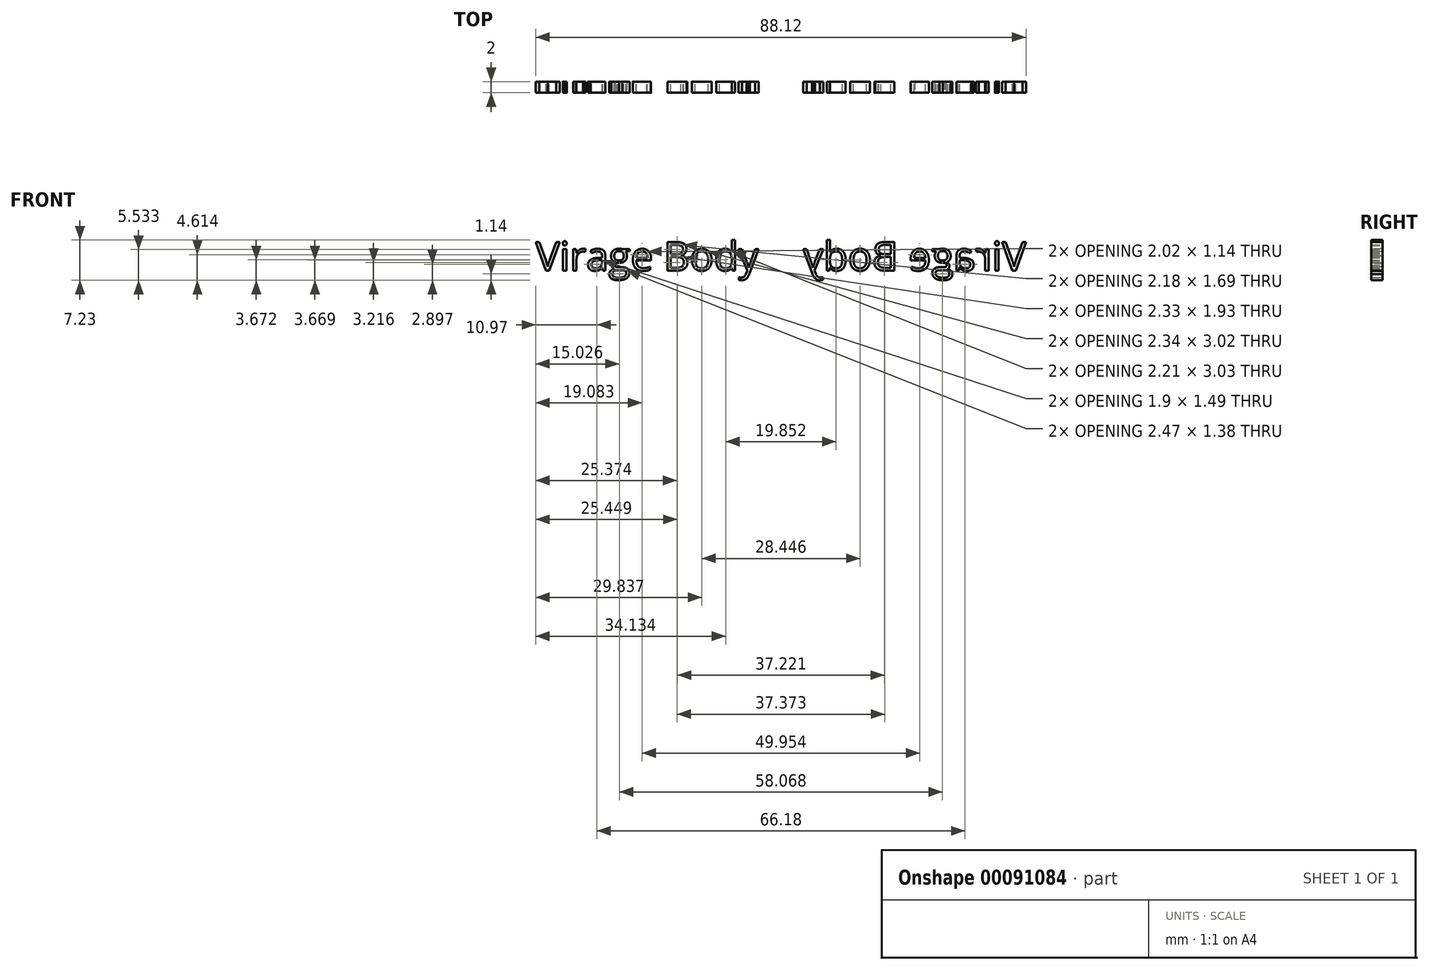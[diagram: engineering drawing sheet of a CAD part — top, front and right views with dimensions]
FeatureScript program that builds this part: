
annotation { "Feature Type Name" : "Feature", "Feature Type Description" : "" }
export const myFeature = defineFeature(function(context is Context, id is Id, definition is map)
    precondition{}
    {
        {
            var Q0;
            Q0=qCreatedBy(makeId("Front.planeOp"),FACE);
            var sketch = newSketch(context, id + "F0", { "sketchPlane" : qUnion([Q0])});
            skText(sketch, "E0", { "text": "Virage Body", "fontName": "OpenSans-Regular.ttf"});
            skLineSegment(sketch, "E1", {"start": v(0, 10.9) * mm, "end": v(0, 9.35) * mm, "construction": true});
            skLineSegment(sketch, "E2", {"start": v(0, 9.35) * mm, "end": v(0, -9.41) * mm, "construction": true});
            skLineSegment(sketch, "E3.MirrorCS", {"start": v(0, -4.2) * mm, "end": v(0, 14.57) * mm, "construction": true});
            const initialGuessF0  = {"E0": [-0.04406, -0.00261, 1, 0, 0.0052]};
            skSetInitialGuess(sketch, initialGuessF0);
            skSolve(sketch);
        }
        {
            var Q0;
            Q0 = qSketchRegion(id + "F0", true);
            extrude(context, id + "F1", {"entities" : qUnion([Q0]), "depth" : 2 * mm});
        }
        {
            var Q0;
            Q0=makeQuery(id+"F1.opExtrude","SWEPT_BODY",BODY,{"disambiguationData":[OSD([sQuery(id+"F0.wireOp",EDGE,"E0.sketch_text.stroke-104"),sQuery(id+"F0.wireOp",EDGE,"E0.sketch_text.stroke-105"),sQuery(id+"F0.wireOp",EDGE,"E0.sketch_text.stroke-106"),sQuery(id+"F0.wireOp",EDGE,"E0.sketch_text.stroke-107")])]});
            var Q1;
            Q1=makeQuery(id+"F1.opExtrude","SWEPT_FACE",FACE,{"disambiguationData":[OSD([sQuery(id+"F0.wireOp",EDGE,"E0.sketch_text.stroke-55")])]});
            var Q2;
            Q2=makeQuery(id+"F1.opExtrude","SWEPT_FACE",FACE,{"disambiguationData":[OSD([sQuery(id+"F0.wireOp",EDGE,"E0.sketch_text.stroke-92")])]});
            var Q3;
            Q3=makeQuery(id+"F1.opExtrude","SWEPT_FACE",FACE,{"disambiguationData":[OSD([sQuery(id+"F0.wireOp",EDGE,"E0.sketch_text.stroke-93")])]});
            var Q4;
            Q4=makeQuery(id+"F1.opExtrude","SWEPT_FACE",FACE,{"disambiguationData":[OSD([sQuery(id+"F0.wireOp",EDGE,"E0.sketch_text.stroke-103")])]});
            var Q5;
            Q5=makeQuery(id+"F1.opExtrude","SWEPT_FACE",FACE,{"disambiguationData":[OSD([sQuery(id+"F0.wireOp",EDGE,"E0.sketch_text.stroke-106")])]});
            var Q6;
            Q6=makeQuery(id+"F1.opExtrude","CAP_FACE",FACE,{"disambiguationData":[OSD([sQuery(id+"F0.wireOp",EDGE,"E0.sketch_text.stroke-105"),sQuery(id+"F0.wireOp",EDGE,"E0.sketch_text.stroke-106"),sQuery(id+"F0.wireOp",EDGE,"E0.sketch_text.stroke-107"),sQuery(id+"F0.wireOp",EDGE,"E0.sketch_text.stroke-108"),sQuery(id+"F0.wireOp",EDGE,"E0.sketch_text.stroke-109"),sQuery(id+"F0.wireOp",EDGE,"E0.sketch_text.stroke-110"),sQuery(id+"F0.wireOp",EDGE,"E0.sketch_text.stroke-111"),sQuery(id+"F0.wireOp",EDGE,"E0.sketch_text.stroke-112"),sQuery(id+"F0.wireOp",EDGE,"E0.sketch_text.stroke-113"),sQuery(id+"F0.wireOp",EDGE,"E0.sketch_text.stroke-114"),sQuery(id+"F0.wireOp",EDGE,"E0.sketch_text.stroke-115"),sQuery(id+"F0.wireOp",EDGE,"E0.sketch_text.stroke-116"),sQuery(id+"F0.wireOp",EDGE,"E0.sketch_text.stroke-117"),sQuery(id+"F0.wireOp",EDGE,"E0.sketch_text.stroke-118"),sQuery(id+"F0.wireOp",EDGE,"E0.sketch_text.stroke-119"),sQuery(id+"F0.wireOp",EDGE,"E0.sketch_text.stroke-120"),sQuery(id+"F0.wireOp",EDGE,"E0.sketch_text.stroke-121"),sQuery(id+"F0.wireOp",EDGE,"E0.sketch_text.stroke-122"),sQuery(id+"F0.wireOp",EDGE,"E0.sketch_text.stroke-123")])],"isStart":true});
            var Q7;
            Q7=makeQuery(id+"F1.opExtrude","SWEPT_FACE",FACE,{"disambiguationData":[OSD([sQuery(id+"F0.wireOp",EDGE,"E0.sketch_text.stroke-162")])]});
            var Q8;
            Q8=makeQuery(id+"F1.opExtrude","CAP_FACE",FACE,{"disambiguationData":[OSD([sQuery(id+"F0.wireOp",EDGE,"E0.sketch_text.stroke-149"),sQuery(id+"F0.wireOp",EDGE,"E0.sketch_text.stroke-150"),sQuery(id+"F0.wireOp",EDGE,"E0.sketch_text.stroke-151"),sQuery(id+"F0.wireOp",EDGE,"E0.sketch_text.stroke-152"),sQuery(id+"F0.wireOp",EDGE,"E0.sketch_text.stroke-153"),sQuery(id+"F0.wireOp",EDGE,"E0.sketch_text.stroke-154"),sQuery(id+"F0.wireOp",EDGE,"E0.sketch_text.stroke-155"),sQuery(id+"F0.wireOp",EDGE,"E0.sketch_text.stroke-156"),sQuery(id+"F0.wireOp",EDGE,"E0.sketch_text.stroke-157"),sQuery(id+"F0.wireOp",EDGE,"E0.sketch_text.stroke-158"),sQuery(id+"F0.wireOp",EDGE,"E0.sketch_text.stroke-159"),sQuery(id+"F0.wireOp",EDGE,"E0.sketch_text.stroke-160"),sQuery(id+"F0.wireOp",EDGE,"E0.sketch_text.stroke-161"),sQuery(id+"F0.wireOp",EDGE,"E0.sketch_text.stroke-162"),sQuery(id+"F0.wireOp",EDGE,"E0.sketch_text.stroke-163"),sQuery(id+"F0.wireOp",EDGE,"E0.sketch_text.stroke-164"),sQuery(id+"F0.wireOp",EDGE,"E0.sketch_text.stroke-165")])],"isStart":false});
            var Q9;
            Q9=makeQuery(id+"F1.opExtrude","SWEPT_FACE",FACE,{"disambiguationData":[OSD([sQuery(id+"F0.wireOp",EDGE,"E0.sketch_text.stroke-163")])]});
            var Q10;
            Q10=makeQuery(id+"F1.opExtrude","SWEPT_FACE",FACE,{"disambiguationData":[OSD([sQuery(id+"F0.wireOp",EDGE,"E0.sketch_text.stroke-147")])]});
            var Q11;
            Q11=makeQuery(id+"F1.opExtrude","SWEPT_FACE",FACE,{"disambiguationData":[OSD([sQuery(id+"F0.wireOp",EDGE,"E0.sketch_text.stroke-148")])]});
            var Q12;
            Q12=makeQuery(id+"F1.opExtrude","SWEPT_FACE",FACE,{"disambiguationData":[OSD([sQuery(id+"F0.wireOp",EDGE,"E0.sketch_text.stroke-149")])]});
            var Q13;
            Q13=makeQuery(id+"F1.opExtrude","SWEPT_FACE",FACE,{"disambiguationData":[OSD([sQuery(id+"F0.wireOp",EDGE,"E0.sketch_text.stroke-150")])]});
            var Q14;
            Q14=makeQuery(id+"F1.opExtrude","SWEPT_FACE",FACE,{"disambiguationData":[OSD([sQuery(id+"F0.wireOp",EDGE,"E0.sketch_text.stroke-151")])]});
            var Q15;
            Q15=makeQuery(id+"F1.opExtrude","SWEPT_FACE",FACE,{"disambiguationData":[OSD([sQuery(id+"F0.wireOp",EDGE,"E0.sketch_text.stroke-155")])]});
            var Q16;
            Q16=makeQuery(id+"F1.opExtrude","SWEPT_FACE",FACE,{"disambiguationData":[OSD([sQuery(id+"F0.wireOp",EDGE,"E0.sketch_text.stroke-156")])]});
            var Q17;
            Q17=makeQuery(id+"F1.opExtrude","SWEPT_FACE",FACE,{"disambiguationData":[OSD([sQuery(id+"F0.wireOp",EDGE,"E0.sketch_text.stroke-158")])]});
            var Q18;
            Q18=makeQuery(id+"F1.opExtrude","SWEPT_FACE",FACE,{"disambiguationData":[OSD([sQuery(id+"F0.wireOp",EDGE,"E0.sketch_text.stroke-160")])]});
            var Q19;
            Q19=makeQuery(id+"F1.opExtrude","SWEPT_FACE",FACE,{"disambiguationData":[OSD([sQuery(id+"F0.wireOp",EDGE,"E0.sketch_text.stroke-146")])]});
            var Q20;
            Q20=makeQuery(id+"F1.opExtrude","CAP_FACE",FACE,{"disambiguationData":[OSD([sQuery(id+"F0.wireOp",EDGE,"E0.sketch_text.stroke-149"),sQuery(id+"F0.wireOp",EDGE,"E0.sketch_text.stroke-150"),sQuery(id+"F0.wireOp",EDGE,"E0.sketch_text.stroke-151"),sQuery(id+"F0.wireOp",EDGE,"E0.sketch_text.stroke-152"),sQuery(id+"F0.wireOp",EDGE,"E0.sketch_text.stroke-153"),sQuery(id+"F0.wireOp",EDGE,"E0.sketch_text.stroke-154"),sQuery(id+"F0.wireOp",EDGE,"E0.sketch_text.stroke-155"),sQuery(id+"F0.wireOp",EDGE,"E0.sketch_text.stroke-156"),sQuery(id+"F0.wireOp",EDGE,"E0.sketch_text.stroke-157"),sQuery(id+"F0.wireOp",EDGE,"E0.sketch_text.stroke-158"),sQuery(id+"F0.wireOp",EDGE,"E0.sketch_text.stroke-159"),sQuery(id+"F0.wireOp",EDGE,"E0.sketch_text.stroke-160"),sQuery(id+"F0.wireOp",EDGE,"E0.sketch_text.stroke-161"),sQuery(id+"F0.wireOp",EDGE,"E0.sketch_text.stroke-162"),sQuery(id+"F0.wireOp",EDGE,"E0.sketch_text.stroke-163"),sQuery(id+"F0.wireOp",EDGE,"E0.sketch_text.stroke-164"),sQuery(id+"F0.wireOp",EDGE,"E0.sketch_text.stroke-165")])],"isStart":true});
            var Q21;
            Q21=makeQuery(id+"F1.opExtrude","SWEPT_FACE",FACE,{"disambiguationData":[OSD([sQuery(id+"F0.wireOp",EDGE,"E0.sketch_text.stroke-132")])]});
            var Q22;
            Q22=makeQuery(id+"F1.opExtrude","SWEPT_FACE",FACE,{"disambiguationData":[OSD([sQuery(id+"F0.wireOp",EDGE,"E0.sketch_text.stroke-133")])]});
            var Q23;
            Q23=makeQuery(id+"F1.opExtrude","SWEPT_FACE",FACE,{"disambiguationData":[OSD([sQuery(id+"F0.wireOp",EDGE,"E0.sketch_text.stroke-134")])]});
            var Q24;
            Q24=makeQuery(id+"F1.opExtrude","SWEPT_FACE",FACE,{"disambiguationData":[OSD([sQuery(id+"F0.wireOp",EDGE,"E0.sketch_text.stroke-135")])]});
            var Q25;
            Q25=makeQuery(id+"F1.opExtrude","SWEPT_FACE",FACE,{"disambiguationData":[OSD([sQuery(id+"F0.wireOp",EDGE,"E0.sketch_text.stroke-136")])]});
            var Q26;
            Q26=makeQuery(id+"F1.opExtrude","CAP_FACE",FACE,{"disambiguationData":[OSD([sQuery(id+"F0.wireOp",EDGE,"E0.sketch_text.stroke-124"),sQuery(id+"F0.wireOp",EDGE,"E0.sketch_text.stroke-125"),sQuery(id+"F0.wireOp",EDGE,"E0.sketch_text.stroke-126"),sQuery(id+"F0.wireOp",EDGE,"E0.sketch_text.stroke-127"),sQuery(id+"F0.wireOp",EDGE,"E0.sketch_text.stroke-128"),sQuery(id+"F0.wireOp",EDGE,"E0.sketch_text.stroke-129"),sQuery(id+"F0.wireOp",EDGE,"E0.sketch_text.stroke-130"),sQuery(id+"F0.wireOp",EDGE,"E0.sketch_text.stroke-131"),sQuery(id+"F0.wireOp",EDGE,"E0.sketch_text.stroke-132"),sQuery(id+"F0.wireOp",EDGE,"E0.sketch_text.stroke-133"),sQuery(id+"F0.wireOp",EDGE,"E0.sketch_text.stroke-134"),sQuery(id+"F0.wireOp",EDGE,"E0.sketch_text.stroke-135"),sQuery(id+"F0.wireOp",EDGE,"E0.sketch_text.stroke-136"),sQuery(id+"F0.wireOp",EDGE,"E0.sketch_text.stroke-137"),sQuery(id+"F0.wireOp",EDGE,"E0.sketch_text.stroke-138"),sQuery(id+"F0.wireOp",EDGE,"E0.sketch_text.stroke-139"),sQuery(id+"F0.wireOp",EDGE,"E0.sketch_text.stroke-140"),sQuery(id+"F0.wireOp",EDGE,"E0.sketch_text.stroke-141"),sQuery(id+"F0.wireOp",EDGE,"E0.sketch_text.stroke-142"),sQuery(id+"F0.wireOp",EDGE,"E0.sketch_text.stroke-143"),sQuery(id+"F0.wireOp",EDGE,"E0.sketch_text.stroke-144"),sQuery(id+"F0.wireOp",EDGE,"E0.sketch_text.stroke-145"),sQuery(id+"F0.wireOp",EDGE,"E0.sketch_text.stroke-146"),sQuery(id+"F0.wireOp",EDGE,"E0.sketch_text.stroke-147"),sQuery(id+"F0.wireOp",EDGE,"E0.sketch_text.stroke-148")])],"isStart":false});
            var Q27;
            Q27=makeQuery(id+"F1.opExtrude","SWEPT_FACE",FACE,{"disambiguationData":[OSD([sQuery(id+"F0.wireOp",EDGE,"E0.sketch_text.stroke-137")])]});
            var Q28;
            Q28=makeQuery(id+"F1.opExtrude","SWEPT_FACE",FACE,{"disambiguationData":[OSD([sQuery(id+"F0.wireOp",EDGE,"E0.sketch_text.stroke-143")])]});
            var Q29;
            Q29=makeQuery(id+"F1.opExtrude","SWEPT_FACE",FACE,{"disambiguationData":[OSD([sQuery(id+"F0.wireOp",EDGE,"E0.sketch_text.stroke-138")])]});
            var Q30;
            Q30=makeQuery(id+"F1.opExtrude","SWEPT_FACE",FACE,{"disambiguationData":[OSD([sQuery(id+"F0.wireOp",EDGE,"E0.sketch_text.stroke-139")])]});
            var Q31;
            Q31=makeQuery(id+"F1.opExtrude","SWEPT_FACE",FACE,{"disambiguationData":[OSD([sQuery(id+"F0.wireOp",EDGE,"E0.sketch_text.stroke-142")])]});
            var Q32;
            Q32=makeQuery(id+"F1.opExtrude","SWEPT_FACE",FACE,{"disambiguationData":[OSD([sQuery(id+"F0.wireOp",EDGE,"E0.sketch_text.stroke-140")])]});
            var Q33;
            Q33=makeQuery(id+"F1.opExtrude","SWEPT_FACE",FACE,{"disambiguationData":[OSD([sQuery(id+"F0.wireOp",EDGE,"E0.sketch_text.stroke-144")])]});
            var Q34;
            Q34=makeQuery(id+"F1.opExtrude","SWEPT_FACE",FACE,{"disambiguationData":[OSD([sQuery(id+"F0.wireOp",EDGE,"E0.sketch_text.stroke-145")])]});
            var Q35;
            Q35=makeQuery(id+"F1.opExtrude","SWEPT_FACE",FACE,{"disambiguationData":[OSD([sQuery(id+"F0.wireOp",EDGE,"E0.sketch_text.stroke-118")])]});
            var Q36;
            Q36=makeQuery(id+"F1.opExtrude","SWEPT_FACE",FACE,{"disambiguationData":[OSD([sQuery(id+"F0.wireOp",EDGE,"E0.sketch_text.stroke-119")])]});
            var Q37;
            Q37=makeQuery(id+"F1.opExtrude","SWEPT_FACE",FACE,{"disambiguationData":[OSD([sQuery(id+"F0.wireOp",EDGE,"E0.sketch_text.stroke-120")])]});
            var Q38;
            Q38=makeQuery(id+"F1.opExtrude","SWEPT_FACE",FACE,{"disambiguationData":[OSD([sQuery(id+"F0.wireOp",EDGE,"E0.sketch_text.stroke-121")])]});
            var Q39;
            Q39=makeQuery(id+"F1.opExtrude","SWEPT_FACE",FACE,{"disambiguationData":[OSD([sQuery(id+"F0.wireOp",EDGE,"E0.sketch_text.stroke-122")])]});
            var Q40;
            Q40=makeQuery(id+"F1.opExtrude","SWEPT_FACE",FACE,{"disambiguationData":[OSD([sQuery(id+"F0.wireOp",EDGE,"E0.sketch_text.stroke-113")])]});
            var Q41;
            Q41=makeQuery(id+"F1.opExtrude","SWEPT_FACE",FACE,{"disambiguationData":[OSD([sQuery(id+"F0.wireOp",EDGE,"E0.sketch_text.stroke-124")])]});
            var Q42;
            Q42=makeQuery(id+"F1.opExtrude","CAP_FACE",FACE,{"disambiguationData":[OSD([sQuery(id+"F0.wireOp",EDGE,"E0.sketch_text.stroke-105"),sQuery(id+"F0.wireOp",EDGE,"E0.sketch_text.stroke-106"),sQuery(id+"F0.wireOp",EDGE,"E0.sketch_text.stroke-107"),sQuery(id+"F0.wireOp",EDGE,"E0.sketch_text.stroke-108"),sQuery(id+"F0.wireOp",EDGE,"E0.sketch_text.stroke-109"),sQuery(id+"F0.wireOp",EDGE,"E0.sketch_text.stroke-110"),sQuery(id+"F0.wireOp",EDGE,"E0.sketch_text.stroke-111"),sQuery(id+"F0.wireOp",EDGE,"E0.sketch_text.stroke-112"),sQuery(id+"F0.wireOp",EDGE,"E0.sketch_text.stroke-113"),sQuery(id+"F0.wireOp",EDGE,"E0.sketch_text.stroke-114"),sQuery(id+"F0.wireOp",EDGE,"E0.sketch_text.stroke-115"),sQuery(id+"F0.wireOp",EDGE,"E0.sketch_text.stroke-116"),sQuery(id+"F0.wireOp",EDGE,"E0.sketch_text.stroke-117"),sQuery(id+"F0.wireOp",EDGE,"E0.sketch_text.stroke-118"),sQuery(id+"F0.wireOp",EDGE,"E0.sketch_text.stroke-119"),sQuery(id+"F0.wireOp",EDGE,"E0.sketch_text.stroke-120"),sQuery(id+"F0.wireOp",EDGE,"E0.sketch_text.stroke-121"),sQuery(id+"F0.wireOp",EDGE,"E0.sketch_text.stroke-122"),sQuery(id+"F0.wireOp",EDGE,"E0.sketch_text.stroke-123")])],"isStart":false});
            var Q43;
            Q43=makeQuery(id+"F1.opExtrude","SWEPT_FACE",FACE,{"disambiguationData":[OSD([sQuery(id+"F0.wireOp",EDGE,"E0.sketch_text.stroke-111")])]});
            var Q44;
            Q44=makeQuery(id+"F1.opExtrude","SWEPT_FACE",FACE,{"disambiguationData":[OSD([sQuery(id+"F0.wireOp",EDGE,"E0.sketch_text.stroke-125")])]});
            var Q45;
            Q45=makeQuery(id+"F1.opExtrude","SWEPT_FACE",FACE,{"disambiguationData":[OSD([sQuery(id+"F0.wireOp",EDGE,"E0.sketch_text.stroke-126")])]});
            var Q46;
            Q46=makeQuery(id+"F1.opExtrude","SWEPT_FACE",FACE,{"disambiguationData":[OSD([sQuery(id+"F0.wireOp",EDGE,"E0.sketch_text.stroke-114")])]});
            var Q47;
            Q47=makeQuery(id+"F1.opExtrude","SWEPT_FACE",FACE,{"disambiguationData":[OSD([sQuery(id+"F0.wireOp",EDGE,"E0.sketch_text.stroke-116")])]});
            var Q48;
            Q48=makeQuery(id+"F1.opExtrude","SWEPT_FACE",FACE,{"disambiguationData":[OSD([sQuery(id+"F0.wireOp",EDGE,"E0.sketch_text.stroke-176")])]});
            var Q49;
            Q49=makeQuery(id+"F1.opExtrude","SWEPT_FACE",FACE,{"disambiguationData":[OSD([sQuery(id+"F0.wireOp",EDGE,"E0.sketch_text.stroke-165")])]});
            var Q50;
            Q50=makeQuery(id+"F1.opExtrude","SWEPT_FACE",FACE,{"disambiguationData":[OSD([sQuery(id+"F0.wireOp",EDGE,"E0.sketch_text.stroke-171")])]});
            var Q51;
            Q51=makeQuery(id+"F1.opExtrude","CAP_FACE",FACE,{"disambiguationData":[OSD([sQuery(id+"F0.wireOp",EDGE,"E0.sketch_text.stroke-166"),sQuery(id+"F0.wireOp",EDGE,"E0.sketch_text.stroke-167"),sQuery(id+"F0.wireOp",EDGE,"E0.sketch_text.stroke-168"),sQuery(id+"F0.wireOp",EDGE,"E0.sketch_text.stroke-169"),sQuery(id+"F0.wireOp",EDGE,"E0.sketch_text.stroke-170"),sQuery(id+"F0.wireOp",EDGE,"E0.sketch_text.stroke-171"),sQuery(id+"F0.wireOp",EDGE,"E0.sketch_text.stroke-172"),sQuery(id+"F0.wireOp",EDGE,"E0.sketch_text.stroke-173"),sQuery(id+"F0.wireOp",EDGE,"E0.sketch_text.stroke-174"),sQuery(id+"F0.wireOp",EDGE,"E0.sketch_text.stroke-175"),sQuery(id+"F0.wireOp",EDGE,"E0.sketch_text.stroke-176"),sQuery(id+"F0.wireOp",EDGE,"E0.sketch_text.stroke-177"),sQuery(id+"F0.wireOp",EDGE,"E0.sketch_text.stroke-178"),sQuery(id+"F0.wireOp",EDGE,"E0.sketch_text.stroke-179"),sQuery(id+"F0.wireOp",EDGE,"E0.sketch_text.stroke-180"),sQuery(id+"F0.wireOp",EDGE,"E0.sketch_text.stroke-181"),sQuery(id+"F0.wireOp",EDGE,"E0.sketch_text.stroke-182"),sQuery(id+"F0.wireOp",EDGE,"E0.sketch_text.stroke-183"),sQuery(id+"F0.wireOp",EDGE,"E0.sketch_text.stroke-184"),sQuery(id+"F0.wireOp",EDGE,"E0.sketch_text.stroke-185"),sQuery(id+"F0.wireOp",EDGE,"E0.sketch_text.stroke-186"),sQuery(id+"F0.wireOp",EDGE,"E0.sketch_text.stroke-187"),sQuery(id+"F0.wireOp",EDGE,"E0.sketch_text.stroke-188"),sQuery(id+"F0.wireOp",EDGE,"E0.sketch_text.stroke-189")])],"isStart":false});
            var Q52;
            Q52=makeQuery(id+"F1.opExtrude","SWEPT_FACE",FACE,{"disambiguationData":[OSD([sQuery(id+"F0.wireOp",EDGE,"E0.sketch_text.stroke-166")])]});
            var Q53;
            Q53=makeQuery(id+"F1.opExtrude","SWEPT_FACE",FACE,{"disambiguationData":[OSD([sQuery(id+"F0.wireOp",EDGE,"E0.sketch_text.stroke-169")])]});
            var Q54;
            Q54=makeQuery(id+"F1.opExtrude","SWEPT_FACE",FACE,{"disambiguationData":[OSD([sQuery(id+"F0.wireOp",EDGE,"E0.sketch_text.stroke-167")])]});
            var Q55;
            Q55=makeQuery(id+"F1.opExtrude","SWEPT_FACE",FACE,{"disambiguationData":[OSD([sQuery(id+"F0.wireOp",EDGE,"E0.sketch_text.stroke-168")])]});
            var Q56;
            Q56=makeQuery(id+"F1.opExtrude","SWEPT_FACE",FACE,{"disambiguationData":[OSD([sQuery(id+"F0.wireOp",EDGE,"E0.sketch_text.stroke-172")])]});
            var Q57;
            Q57=makeQuery(id+"F1.opExtrude","SWEPT_FACE",FACE,{"disambiguationData":[OSD([sQuery(id+"F0.wireOp",EDGE,"E0.sketch_text.stroke-173")])]});
            var Q58;
            Q58=makeQuery(id+"F1.opExtrude","SWEPT_FACE",FACE,{"disambiguationData":[OSD([sQuery(id+"F0.wireOp",EDGE,"E0.sketch_text.stroke-174")])]});
            var Q59;
            Q59=makeQuery(id+"F1.opExtrude","SWEPT_FACE",FACE,{"disambiguationData":[OSD([sQuery(id+"F0.wireOp",EDGE,"E0.sketch_text.stroke-177")])]});
            var Q60;
            Q60=makeQuery(id+"F1.opExtrude","SWEPT_FACE",FACE,{"disambiguationData":[OSD([sQuery(id+"F0.wireOp",EDGE,"E0.sketch_text.stroke-193")])]});
            var Q61;
            Q61=makeQuery(id+"F1.opExtrude","SWEPT_FACE",FACE,{"disambiguationData":[OSD([sQuery(id+"F0.wireOp",EDGE,"E0.sketch_text.stroke-194")])]});
            var Q62;
            Q62=makeQuery(id+"F1.opExtrude","SWEPT_FACE",FACE,{"disambiguationData":[OSD([sQuery(id+"F0.wireOp",EDGE,"E0.sketch_text.stroke-180")])]});
            var Q63;
            Q63=makeQuery(id+"F1.opExtrude","SWEPT_FACE",FACE,{"disambiguationData":[OSD([sQuery(id+"F0.wireOp",EDGE,"E0.sketch_text.stroke-183")])]});
            var Q64;
            Q64=makeQuery(id+"F1.opExtrude","SWEPT_FACE",FACE,{"disambiguationData":[OSD([sQuery(id+"F0.wireOp",EDGE,"E0.sketch_text.stroke-182")])]});
            var Q65;
            Q65=makeQuery(id+"F1.opExtrude","SWEPT_FACE",FACE,{"disambiguationData":[OSD([sQuery(id+"F0.wireOp",EDGE,"E0.sketch_text.stroke-53")])]});
            var Q66;
            Q66=makeQuery(id+"F1.opExtrude","SWEPT_FACE",FACE,{"disambiguationData":[OSD([sQuery(id+"F0.wireOp",EDGE,"E0.sketch_text.stroke-54")])]});
            var Q67;
            Q67=makeQuery(id+"F1.opExtrude","SWEPT_FACE",FACE,{"disambiguationData":[OSD([sQuery(id+"F0.wireOp",EDGE,"E0.sketch_text.stroke-164")])]});
            var Q68;
            Q68=makeQuery(id+"F1.opExtrude","SWEPT_FACE",FACE,{"disambiguationData":[OSD([sQuery(id+"F0.wireOp",EDGE,"E0.sketch_text.stroke-157")])]});
            var Q69;
            Q69=makeQuery(id+"F1.opExtrude","SWEPT_FACE",FACE,{"disambiguationData":[OSD([sQuery(id+"F0.wireOp",EDGE,"E0.sketch_text.stroke-153")])]});
            var Q70;
            Q70=makeQuery(id+"F1.opExtrude","SWEPT_FACE",FACE,{"disambiguationData":[OSD([sQuery(id+"F0.wireOp",EDGE,"E0.sketch_text.stroke-154")])]});
            var Q71;
            Q71=makeQuery(id+"F1.opExtrude","SWEPT_FACE",FACE,{"disambiguationData":[OSD([sQuery(id+"F0.wireOp",EDGE,"E0.sketch_text.stroke-159")])]});
            var Q72;
            Q72=makeQuery(id+"F1.opExtrude","SWEPT_FACE",FACE,{"disambiguationData":[OSD([sQuery(id+"F0.wireOp",EDGE,"E0.sketch_text.stroke-161")])]});
            var Q73;
            Q73=makeQuery(id+"F1.opExtrude","SWEPT_FACE",FACE,{"disambiguationData":[OSD([sQuery(id+"F0.wireOp",EDGE,"E0.sketch_text.stroke-141")])]});
            var Q74;
            Q74=makeQuery(id+"F1.opExtrude","SWEPT_FACE",FACE,{"disambiguationData":[OSD([sQuery(id+"F0.wireOp",EDGE,"E0.sketch_text.stroke-127")])]});
            var Q75;
            Q75=makeQuery(id+"F1.opExtrude","CAP_FACE",FACE,{"disambiguationData":[OSD([sQuery(id+"F0.wireOp",EDGE,"E0.sketch_text.stroke-124"),sQuery(id+"F0.wireOp",EDGE,"E0.sketch_text.stroke-125"),sQuery(id+"F0.wireOp",EDGE,"E0.sketch_text.stroke-126"),sQuery(id+"F0.wireOp",EDGE,"E0.sketch_text.stroke-127"),sQuery(id+"F0.wireOp",EDGE,"E0.sketch_text.stroke-128"),sQuery(id+"F0.wireOp",EDGE,"E0.sketch_text.stroke-129"),sQuery(id+"F0.wireOp",EDGE,"E0.sketch_text.stroke-130"),sQuery(id+"F0.wireOp",EDGE,"E0.sketch_text.stroke-131"),sQuery(id+"F0.wireOp",EDGE,"E0.sketch_text.stroke-132"),sQuery(id+"F0.wireOp",EDGE,"E0.sketch_text.stroke-133"),sQuery(id+"F0.wireOp",EDGE,"E0.sketch_text.stroke-134"),sQuery(id+"F0.wireOp",EDGE,"E0.sketch_text.stroke-135"),sQuery(id+"F0.wireOp",EDGE,"E0.sketch_text.stroke-136"),sQuery(id+"F0.wireOp",EDGE,"E0.sketch_text.stroke-137"),sQuery(id+"F0.wireOp",EDGE,"E0.sketch_text.stroke-138"),sQuery(id+"F0.wireOp",EDGE,"E0.sketch_text.stroke-139"),sQuery(id+"F0.wireOp",EDGE,"E0.sketch_text.stroke-140"),sQuery(id+"F0.wireOp",EDGE,"E0.sketch_text.stroke-141"),sQuery(id+"F0.wireOp",EDGE,"E0.sketch_text.stroke-142"),sQuery(id+"F0.wireOp",EDGE,"E0.sketch_text.stroke-143"),sQuery(id+"F0.wireOp",EDGE,"E0.sketch_text.stroke-144"),sQuery(id+"F0.wireOp",EDGE,"E0.sketch_text.stroke-145"),sQuery(id+"F0.wireOp",EDGE,"E0.sketch_text.stroke-146"),sQuery(id+"F0.wireOp",EDGE,"E0.sketch_text.stroke-147"),sQuery(id+"F0.wireOp",EDGE,"E0.sketch_text.stroke-148")])],"isStart":true});
            var Q76;
            Q76=makeQuery(id+"F1.opExtrude","SWEPT_FACE",FACE,{"disambiguationData":[OSD([sQuery(id+"F0.wireOp",EDGE,"E0.sketch_text.stroke-128")])]});
            var Q77;
            Q77=makeQuery(id+"F1.opExtrude","SWEPT_FACE",FACE,{"disambiguationData":[OSD([sQuery(id+"F0.wireOp",EDGE,"E0.sketch_text.stroke-131")])]});
            var Q78;
            Q78=makeQuery(id+"F1.opExtrude","SWEPT_FACE",FACE,{"disambiguationData":[OSD([sQuery(id+"F0.wireOp",EDGE,"E0.sketch_text.stroke-123")])]});
            var Q79;
            Q79=makeQuery(id+"F1.opExtrude","SWEPT_FACE",FACE,{"disambiguationData":[OSD([sQuery(id+"F0.wireOp",EDGE,"E0.sketch_text.stroke-109")])]});
            var Q80;
            Q80=makeQuery(id+"F1.opExtrude","SWEPT_FACE",FACE,{"disambiguationData":[OSD([sQuery(id+"F0.wireOp",EDGE,"E0.sketch_text.stroke-112")])]});
            var Q81;
            Q81=makeQuery(id+"F1.opExtrude","SWEPT_FACE",FACE,{"disambiguationData":[OSD([sQuery(id+"F0.wireOp",EDGE,"E0.sketch_text.stroke-110")])]});
            var Q82;
            Q82=makeQuery(id+"F1.opExtrude","SWEPT_FACE",FACE,{"disambiguationData":[OSD([sQuery(id+"F0.wireOp",EDGE,"E0.sketch_text.stroke-115")])]});
            var Q83;
            Q83=makeQuery(id+"F1.opExtrude","SWEPT_FACE",FACE,{"disambiguationData":[OSD([sQuery(id+"F0.wireOp",EDGE,"E0.sketch_text.stroke-117")])]});
            var Q84;
            Q84=makeQuery(id+"F1.opExtrude","SWEPT_FACE",FACE,{"disambiguationData":[OSD([sQuery(id+"F0.wireOp",EDGE,"E0.sketch_text.stroke-170")])]});
            var Q85;
            Q85=makeQuery(id+"F1.opExtrude","SWEPT_FACE",FACE,{"disambiguationData":[OSD([sQuery(id+"F0.wireOp",EDGE,"E0.sketch_text.stroke-175")])]});
            var Q86;
            Q86=makeQuery(id+"F1.opExtrude","SWEPT_FACE",FACE,{"disambiguationData":[OSD([sQuery(id+"F0.wireOp",EDGE,"E0.sketch_text.stroke-178")])]});
            var Q87;
            Q87=makeQuery(id+"F1.opExtrude","SWEPT_FACE",FACE,{"disambiguationData":[OSD([sQuery(id+"F0.wireOp",EDGE,"E0.sketch_text.stroke-185")])]});
            var Q88;
            Q88=makeQuery(id+"F1.opExtrude","SWEPT_FACE",FACE,{"disambiguationData":[OSD([sQuery(id+"F0.wireOp",EDGE,"E0.sketch_text.stroke-195")])]});
            var Q89;
            Q89=makeQuery(id+"F1.opExtrude","SWEPT_FACE",FACE,{"disambiguationData":[OSD([sQuery(id+"F0.wireOp",EDGE,"E0.sketch_text.stroke-181")])]});
            var Q90;
            Q90=makeQuery(id+"F1.opExtrude","SWEPT_FACE",FACE,{"disambiguationData":[OSD([sQuery(id+"F0.wireOp",EDGE,"E0.sketch_text.stroke-184")])]});
            var Q91;
            Q91=makeQuery(id+"F1.opExtrude","SWEPT_FACE",FACE,{"disambiguationData":[OSD([sQuery(id+"F0.wireOp",EDGE,"E0.sketch_text.stroke-152")])]});
            var Q92;
            Q92=makeQuery(id+"F1.opExtrude","SWEPT_FACE",FACE,{"disambiguationData":[OSD([sQuery(id+"F0.wireOp",EDGE,"E0.sketch_text.stroke-129")])]});
            var Q93;
            Q93=makeQuery(id+"F1.opExtrude","SWEPT_FACE",FACE,{"disambiguationData":[OSD([sQuery(id+"F0.wireOp",EDGE,"E0.sketch_text.stroke-108")])]});
            var Q94;
            Q94=makeQuery(id+"F1.opExtrude","SWEPT_FACE",FACE,{"disambiguationData":[OSD([sQuery(id+"F0.wireOp",EDGE,"E0.sketch_text.stroke-179")])]});
            var Q95;
            Q95=makeQuery(id+"F1.opExtrude","SWEPT_FACE",FACE,{"disambiguationData":[OSD([sQuery(id+"F0.wireOp",EDGE,"E0.sketch_text.stroke-130")])]});
            var Q96;
            Q96=makeQuery(id+"F1.opExtrude","CAP_FACE",FACE,{"disambiguationData":[OSD([sQuery(id+"F0.wireOp",EDGE,"E0.sketch_text.stroke-61"),sQuery(id+"F0.wireOp",EDGE,"E0.sketch_text.stroke-62"),sQuery(id+"F0.wireOp",EDGE,"E0.sketch_text.stroke-63"),sQuery(id+"F0.wireOp",EDGE,"E0.sketch_text.stroke-64"),sQuery(id+"F0.wireOp",EDGE,"E0.sketch_text.stroke-65"),sQuery(id+"F0.wireOp",EDGE,"E0.sketch_text.stroke-66"),sQuery(id+"F0.wireOp",EDGE,"E0.sketch_text.stroke-67"),sQuery(id+"F0.wireOp",EDGE,"E0.sketch_text.stroke-68"),sQuery(id+"F0.wireOp",EDGE,"E0.sketch_text.stroke-69"),sQuery(id+"F0.wireOp",EDGE,"E0.sketch_text.stroke-70"),sQuery(id+"F0.wireOp",EDGE,"E0.sketch_text.stroke-71"),sQuery(id+"F0.wireOp",EDGE,"E0.sketch_text.stroke-72"),sQuery(id+"F0.wireOp",EDGE,"E0.sketch_text.stroke-73"),sQuery(id+"F0.wireOp",EDGE,"E0.sketch_text.stroke-74"),sQuery(id+"F0.wireOp",EDGE,"E0.sketch_text.stroke-75"),sQuery(id+"F0.wireOp",EDGE,"E0.sketch_text.stroke-76"),sQuery(id+"F0.wireOp",EDGE,"E0.sketch_text.stroke-77"),sQuery(id+"F0.wireOp",EDGE,"E0.sketch_text.stroke-78"),sQuery(id+"F0.wireOp",EDGE,"E0.sketch_text.stroke-79"),sQuery(id+"F0.wireOp",EDGE,"E0.sketch_text.stroke-80"),sQuery(id+"F0.wireOp",EDGE,"E0.sketch_text.stroke-81"),sQuery(id+"F0.wireOp",EDGE,"E0.sketch_text.stroke-82"),sQuery(id+"F0.wireOp",EDGE,"E0.sketch_text.stroke-83"),sQuery(id+"F0.wireOp",EDGE,"E0.sketch_text.stroke-84"),sQuery(id+"F0.wireOp",EDGE,"E0.sketch_text.stroke-85"),sQuery(id+"F0.wireOp",EDGE,"E0.sketch_text.stroke-86"),sQuery(id+"F0.wireOp",EDGE,"E0.sketch_text.stroke-87"),sQuery(id+"F0.wireOp",EDGE,"E0.sketch_text.stroke-88"),sQuery(id+"F0.wireOp",EDGE,"E0.sketch_text.stroke-89"),sQuery(id+"F0.wireOp",EDGE,"E0.sketch_text.stroke-90"),sQuery(id+"F0.wireOp",EDGE,"E0.sketch_text.stroke-91"),sQuery(id+"F0.wireOp",EDGE,"E0.sketch_text.stroke-92"),sQuery(id+"F0.wireOp",EDGE,"E0.sketch_text.stroke-93"),sQuery(id+"F0.wireOp",EDGE,"E0.sketch_text.stroke-94"),sQuery(id+"F0.wireOp",EDGE,"E0.sketch_text.stroke-95"),sQuery(id+"F0.wireOp",EDGE,"E0.sketch_text.stroke-96"),sQuery(id+"F0.wireOp",EDGE,"E0.sketch_text.stroke-97"),sQuery(id+"F0.wireOp",EDGE,"E0.sketch_text.stroke-98"),sQuery(id+"F0.wireOp",EDGE,"E0.sketch_text.stroke-99"),sQuery(id+"F0.wireOp",EDGE,"E0.sketch_text.stroke-100"),sQuery(id+"F0.wireOp",EDGE,"E0.sketch_text.stroke-101"),sQuery(id+"F0.wireOp",EDGE,"E0.sketch_text.stroke-102"),sQuery(id+"F0.wireOp",EDGE,"E0.sketch_text.stroke-103"),sQuery(id+"F0.wireOp",EDGE,"E0.sketch_text.stroke-104")])],"isStart":false});
            var Q97;
            Q97=makeQuery(id+"F1.opExtrude","SWEPT_FACE",FACE,{"disambiguationData":[OSD([sQuery(id+"F0.wireOp",EDGE,"E0.sketch_text.stroke-76")])]});
            var Q98;
            Q98=makeQuery(id+"F1.opExtrude","SWEPT_FACE",FACE,{"disambiguationData":[OSD([sQuery(id+"F0.wireOp",EDGE,"E0.sketch_text.stroke-62")])]});
            var Q99;
            Q99=makeQuery(id+"F1.opExtrude","SWEPT_FACE",FACE,{"disambiguationData":[OSD([sQuery(id+"F0.wireOp",EDGE,"E0.sketch_text.stroke-63")])]});
            var Q100;
            Q100=makeQuery(id+"F1.opExtrude","SWEPT_FACE",FACE,{"disambiguationData":[OSD([sQuery(id+"F0.wireOp",EDGE,"E0.sketch_text.stroke-80")])]});
            var Q101;
            Q101=makeQuery(id+"F1.opExtrude","SWEPT_FACE",FACE,{"disambiguationData":[OSD([sQuery(id+"F0.wireOp",EDGE,"E0.sketch_text.stroke-64")])]});
            var Q102;
            Q102=makeQuery(id+"F1.opExtrude","SWEPT_FACE",FACE,{"disambiguationData":[OSD([sQuery(id+"F0.wireOp",EDGE,"E0.sketch_text.stroke-65")])]});
            var Q103;
            Q103=makeQuery(id+"F1.opExtrude","SWEPT_FACE",FACE,{"disambiguationData":[OSD([sQuery(id+"F0.wireOp",EDGE,"E0.sketch_text.stroke-66")])]});
            var Q104;
            Q104=makeQuery(id+"F1.opExtrude","SWEPT_FACE",FACE,{"disambiguationData":[OSD([sQuery(id+"F0.wireOp",EDGE,"E0.sketch_text.stroke-69")])]});
            var Q105;
            Q105=makeQuery(id+"F1.opExtrude","SWEPT_FACE",FACE,{"disambiguationData":[OSD([sQuery(id+"F0.wireOp",EDGE,"E0.sketch_text.stroke-83")])]});
            var Q106;
            Q106=makeQuery(id+"F1.opExtrude","SWEPT_FACE",FACE,{"disambiguationData":[OSD([sQuery(id+"F0.wireOp",EDGE,"E0.sketch_text.stroke-68")])]});
            var Q107;
            Q107=makeQuery(id+"F1.opExtrude","SWEPT_FACE",FACE,{"disambiguationData":[OSD([sQuery(id+"F0.wireOp",EDGE,"E0.sketch_text.stroke-46")])]});
            var Q108;
            Q108=makeQuery(id+"F1.opExtrude","SWEPT_FACE",FACE,{"disambiguationData":[OSD([sQuery(id+"F0.wireOp",EDGE,"E0.sketch_text.stroke-48")])]});
            var Q109;
            Q109=makeQuery(id+"F1.opExtrude","SWEPT_FACE",FACE,{"disambiguationData":[OSD([sQuery(id+"F0.wireOp",EDGE,"E0.sketch_text.stroke-49")])]});
            var Q110;
            Q110=makeQuery(id+"F1.opExtrude","SWEPT_FACE",FACE,{"disambiguationData":[OSD([sQuery(id+"F0.wireOp",EDGE,"E0.sketch_text.stroke-50")])]});
            var Q111;
            Q111=makeQuery(id+"F1.opExtrude","SWEPT_FACE",FACE,{"disambiguationData":[OSD([sQuery(id+"F0.wireOp",EDGE,"E0.sketch_text.stroke-51")])]});
            var Q112;
            Q112=makeQuery(id+"F1.opExtrude","SWEPT_FACE",FACE,{"disambiguationData":[OSD([sQuery(id+"F0.wireOp",EDGE,"E0.sketch_text.stroke-56")])]});
            var Q113;
            Q113=makeQuery(id+"F1.opExtrude","CAP_FACE",FACE,{"disambiguationData":[OSD([sQuery(id+"F0.wireOp",EDGE,"E0.sketch_text.stroke-34"),sQuery(id+"F0.wireOp",EDGE,"E0.sketch_text.stroke-35"),sQuery(id+"F0.wireOp",EDGE,"E0.sketch_text.stroke-36"),sQuery(id+"F0.wireOp",EDGE,"E0.sketch_text.stroke-37"),sQuery(id+"F0.wireOp",EDGE,"E0.sketch_text.stroke-38"),sQuery(id+"F0.wireOp",EDGE,"E0.sketch_text.stroke-39"),sQuery(id+"F0.wireOp",EDGE,"E0.sketch_text.stroke-40"),sQuery(id+"F0.wireOp",EDGE,"E0.sketch_text.stroke-41"),sQuery(id+"F0.wireOp",EDGE,"E0.sketch_text.stroke-42"),sQuery(id+"F0.wireOp",EDGE,"E0.sketch_text.stroke-43"),sQuery(id+"F0.wireOp",EDGE,"E0.sketch_text.stroke-44"),sQuery(id+"F0.wireOp",EDGE,"E0.sketch_text.stroke-45"),sQuery(id+"F0.wireOp",EDGE,"E0.sketch_text.stroke-46"),sQuery(id+"F0.wireOp",EDGE,"E0.sketch_text.stroke-47"),sQuery(id+"F0.wireOp",EDGE,"E0.sketch_text.stroke-48"),sQuery(id+"F0.wireOp",EDGE,"E0.sketch_text.stroke-49"),sQuery(id+"F0.wireOp",EDGE,"E0.sketch_text.stroke-50"),sQuery(id+"F0.wireOp",EDGE,"E0.sketch_text.stroke-51"),sQuery(id+"F0.wireOp",EDGE,"E0.sketch_text.stroke-52"),sQuery(id+"F0.wireOp",EDGE,"E0.sketch_text.stroke-53"),sQuery(id+"F0.wireOp",EDGE,"E0.sketch_text.stroke-54"),sQuery(id+"F0.wireOp",EDGE,"E0.sketch_text.stroke-55"),sQuery(id+"F0.wireOp",EDGE,"E0.sketch_text.stroke-56"),sQuery(id+"F0.wireOp",EDGE,"E0.sketch_text.stroke-57"),sQuery(id+"F0.wireOp",EDGE,"E0.sketch_text.stroke-58"),sQuery(id+"F0.wireOp",EDGE,"E0.sketch_text.stroke-59"),sQuery(id+"F0.wireOp",EDGE,"E0.sketch_text.stroke-60")])],"isStart":true});
            var Q114;
            Q114=makeQuery(id+"F1.opExtrude","CAP_FACE",FACE,{"disambiguationData":[OSD([sQuery(id+"F0.wireOp",EDGE,"E0.sketch_text.stroke-34"),sQuery(id+"F0.wireOp",EDGE,"E0.sketch_text.stroke-35"),sQuery(id+"F0.wireOp",EDGE,"E0.sketch_text.stroke-36"),sQuery(id+"F0.wireOp",EDGE,"E0.sketch_text.stroke-37"),sQuery(id+"F0.wireOp",EDGE,"E0.sketch_text.stroke-38"),sQuery(id+"F0.wireOp",EDGE,"E0.sketch_text.stroke-39"),sQuery(id+"F0.wireOp",EDGE,"E0.sketch_text.stroke-40"),sQuery(id+"F0.wireOp",EDGE,"E0.sketch_text.stroke-41"),sQuery(id+"F0.wireOp",EDGE,"E0.sketch_text.stroke-42"),sQuery(id+"F0.wireOp",EDGE,"E0.sketch_text.stroke-43"),sQuery(id+"F0.wireOp",EDGE,"E0.sketch_text.stroke-44"),sQuery(id+"F0.wireOp",EDGE,"E0.sketch_text.stroke-45"),sQuery(id+"F0.wireOp",EDGE,"E0.sketch_text.stroke-46"),sQuery(id+"F0.wireOp",EDGE,"E0.sketch_text.stroke-47"),sQuery(id+"F0.wireOp",EDGE,"E0.sketch_text.stroke-48"),sQuery(id+"F0.wireOp",EDGE,"E0.sketch_text.stroke-49"),sQuery(id+"F0.wireOp",EDGE,"E0.sketch_text.stroke-50"),sQuery(id+"F0.wireOp",EDGE,"E0.sketch_text.stroke-51"),sQuery(id+"F0.wireOp",EDGE,"E0.sketch_text.stroke-52"),sQuery(id+"F0.wireOp",EDGE,"E0.sketch_text.stroke-53"),sQuery(id+"F0.wireOp",EDGE,"E0.sketch_text.stroke-54"),sQuery(id+"F0.wireOp",EDGE,"E0.sketch_text.stroke-55"),sQuery(id+"F0.wireOp",EDGE,"E0.sketch_text.stroke-56"),sQuery(id+"F0.wireOp",EDGE,"E0.sketch_text.stroke-57"),sQuery(id+"F0.wireOp",EDGE,"E0.sketch_text.stroke-58"),sQuery(id+"F0.wireOp",EDGE,"E0.sketch_text.stroke-59"),sQuery(id+"F0.wireOp",EDGE,"E0.sketch_text.stroke-60")])],"isStart":false});
            var Q115;
            Q115=makeQuery(id+"F1.opExtrude","SWEPT_FACE",FACE,{"disambiguationData":[OSD([sQuery(id+"F0.wireOp",EDGE,"E0.sketch_text.stroke-44")])]});
            var Q116;
            Q116=makeQuery(id+"F1.opExtrude","SWEPT_FACE",FACE,{"disambiguationData":[OSD([sQuery(id+"F0.wireOp",EDGE,"E0.sketch_text.stroke-90")])]});
            var Q117;
            Q117=makeQuery(id+"F1.opExtrude","SWEPT_FACE",FACE,{"disambiguationData":[OSD([sQuery(id+"F0.wireOp",EDGE,"E0.sketch_text.stroke-91")])]});
            var Q118;
            Q118=makeQuery(id+"F1.opExtrude","SWEPT_FACE",FACE,{"disambiguationData":[OSD([sQuery(id+"F0.wireOp",EDGE,"E0.sketch_text.stroke-94")])]});
            var Q119;
            Q119=makeQuery(id+"F1.opExtrude","SWEPT_FACE",FACE,{"disambiguationData":[OSD([sQuery(id+"F0.wireOp",EDGE,"E0.sketch_text.stroke-101")])]});
            var Q120;
            Q120=makeQuery(id+"F1.opExtrude","SWEPT_FACE",FACE,{"disambiguationData":[OSD([sQuery(id+"F0.wireOp",EDGE,"E0.sketch_text.stroke-87")])]});
            var Q121;
            Q121=makeQuery(id+"F1.opExtrude","SWEPT_FACE",FACE,{"disambiguationData":[OSD([sQuery(id+"F0.wireOp",EDGE,"E0.sketch_text.stroke-99")])]});
            var Q122;
            Q122=makeQuery(id+"F1.opExtrude","SWEPT_FACE",FACE,{"disambiguationData":[OSD([sQuery(id+"F0.wireOp",EDGE,"E0.sketch_text.stroke-100")])]});
            var Q123;
            Q123=makeQuery(id+"F1.opExtrude","SWEPT_FACE",FACE,{"disambiguationData":[OSD([sQuery(id+"F0.wireOp",EDGE,"E0.sketch_text.stroke-98")])]});
            var Q124;
            Q124=makeQuery(id+"F1.opExtrude","SWEPT_FACE",FACE,{"disambiguationData":[OSD([sQuery(id+"F0.wireOp",EDGE,"E0.sketch_text.stroke-102")])]});
            var Q125;
            Q125=makeQuery(id+"F1.opExtrude","CAP_FACE",FACE,{"disambiguationData":[OSD([sQuery(id+"F0.wireOp",EDGE,"E0.sketch_text.stroke-61"),sQuery(id+"F0.wireOp",EDGE,"E0.sketch_text.stroke-62"),sQuery(id+"F0.wireOp",EDGE,"E0.sketch_text.stroke-63"),sQuery(id+"F0.wireOp",EDGE,"E0.sketch_text.stroke-64"),sQuery(id+"F0.wireOp",EDGE,"E0.sketch_text.stroke-65"),sQuery(id+"F0.wireOp",EDGE,"E0.sketch_text.stroke-66"),sQuery(id+"F0.wireOp",EDGE,"E0.sketch_text.stroke-67"),sQuery(id+"F0.wireOp",EDGE,"E0.sketch_text.stroke-68"),sQuery(id+"F0.wireOp",EDGE,"E0.sketch_text.stroke-69"),sQuery(id+"F0.wireOp",EDGE,"E0.sketch_text.stroke-70"),sQuery(id+"F0.wireOp",EDGE,"E0.sketch_text.stroke-71"),sQuery(id+"F0.wireOp",EDGE,"E0.sketch_text.stroke-72"),sQuery(id+"F0.wireOp",EDGE,"E0.sketch_text.stroke-73"),sQuery(id+"F0.wireOp",EDGE,"E0.sketch_text.stroke-74"),sQuery(id+"F0.wireOp",EDGE,"E0.sketch_text.stroke-75"),sQuery(id+"F0.wireOp",EDGE,"E0.sketch_text.stroke-76"),sQuery(id+"F0.wireOp",EDGE,"E0.sketch_text.stroke-77"),sQuery(id+"F0.wireOp",EDGE,"E0.sketch_text.stroke-78"),sQuery(id+"F0.wireOp",EDGE,"E0.sketch_text.stroke-79"),sQuery(id+"F0.wireOp",EDGE,"E0.sketch_text.stroke-80"),sQuery(id+"F0.wireOp",EDGE,"E0.sketch_text.stroke-81"),sQuery(id+"F0.wireOp",EDGE,"E0.sketch_text.stroke-82"),sQuery(id+"F0.wireOp",EDGE,"E0.sketch_text.stroke-83"),sQuery(id+"F0.wireOp",EDGE,"E0.sketch_text.stroke-84"),sQuery(id+"F0.wireOp",EDGE,"E0.sketch_text.stroke-85"),sQuery(id+"F0.wireOp",EDGE,"E0.sketch_text.stroke-86"),sQuery(id+"F0.wireOp",EDGE,"E0.sketch_text.stroke-87"),sQuery(id+"F0.wireOp",EDGE,"E0.sketch_text.stroke-88"),sQuery(id+"F0.wireOp",EDGE,"E0.sketch_text.stroke-89"),sQuery(id+"F0.wireOp",EDGE,"E0.sketch_text.stroke-90"),sQuery(id+"F0.wireOp",EDGE,"E0.sketch_text.stroke-91"),sQuery(id+"F0.wireOp",EDGE,"E0.sketch_text.stroke-92"),sQuery(id+"F0.wireOp",EDGE,"E0.sketch_text.stroke-93"),sQuery(id+"F0.wireOp",EDGE,"E0.sketch_text.stroke-94"),sQuery(id+"F0.wireOp",EDGE,"E0.sketch_text.stroke-95"),sQuery(id+"F0.wireOp",EDGE,"E0.sketch_text.stroke-96"),sQuery(id+"F0.wireOp",EDGE,"E0.sketch_text.stroke-97"),sQuery(id+"F0.wireOp",EDGE,"E0.sketch_text.stroke-98"),sQuery(id+"F0.wireOp",EDGE,"E0.sketch_text.stroke-99"),sQuery(id+"F0.wireOp",EDGE,"E0.sketch_text.stroke-100"),sQuery(id+"F0.wireOp",EDGE,"E0.sketch_text.stroke-101"),sQuery(id+"F0.wireOp",EDGE,"E0.sketch_text.stroke-102"),sQuery(id+"F0.wireOp",EDGE,"E0.sketch_text.stroke-103"),sQuery(id+"F0.wireOp",EDGE,"E0.sketch_text.stroke-104")])],"isStart":true});
            var Q126;
            Q126=makeQuery(id+"F1.opExtrude","SWEPT_FACE",FACE,{"disambiguationData":[OSD([sQuery(id+"F0.wireOp",EDGE,"E0.sketch_text.stroke-88")])]});
            var Q127;
            Q127=makeQuery(id+"F1.opExtrude","SWEPT_FACE",FACE,{"disambiguationData":[OSD([sQuery(id+"F0.wireOp",EDGE,"E0.sketch_text.stroke-89")])]});
            var Q128;
            Q128=makeQuery(id+"F1.opExtrude","SWEPT_FACE",FACE,{"disambiguationData":[OSD([sQuery(id+"F0.wireOp",EDGE,"E0.sketch_text.stroke-105")])]});
            var Q129;
            Q129=makeQuery(id+"F1.opExtrude","SWEPT_FACE",FACE,{"disambiguationData":[OSD([sQuery(id+"F0.wireOp",EDGE,"E0.sketch_text.stroke-107")])]});
            var Q130;
            Q130=makeQuery(id+"F1.opExtrude","SWEPT_FACE",FACE,{"disambiguationData":[OSD([sQuery(id+"F0.wireOp",EDGE,"E0.sketch_text.stroke-104")])]});
            var Q131;
            Q131=makeQuery(id+"F1.opExtrude","SWEPT_FACE",FACE,{"disambiguationData":[OSD([sQuery(id+"F0.wireOp",EDGE,"E0.sketch_text.stroke-18")])]});
            var Q132;
            Q132=makeQuery(id+"F1.opExtrude","SWEPT_FACE",FACE,{"disambiguationData":[OSD([sQuery(id+"F0.wireOp",EDGE,"E0.sketch_text.stroke-23")])]});
            var Q133;
            Q133=makeQuery(id+"F1.opExtrude","SWEPT_FACE",FACE,{"disambiguationData":[OSD([sQuery(id+"F0.wireOp",EDGE,"E0.sketch_text.stroke-13")])]});
            var Q134;
            Q134=makeQuery(id+"F1.opExtrude","SWEPT_FACE",FACE,{"disambiguationData":[OSD([sQuery(id+"F0.wireOp",EDGE,"E0.sketch_text.stroke-11")])]});
            var Q135;
            Q135=makeQuery(id+"F1.opExtrude","CAP_FACE",FACE,{"disambiguationData":[OSD([sQuery(id+"F0.wireOp",EDGE,"E0.sketch_text.stroke-0"),sQuery(id+"F0.wireOp",EDGE,"E0.sketch_text.stroke-1"),sQuery(id+"F0.wireOp",EDGE,"E0.sketch_text.stroke-2"),sQuery(id+"F0.wireOp",EDGE,"E0.sketch_text.stroke-3"),sQuery(id+"F0.wireOp",EDGE,"E0.sketch_text.stroke-4"),sQuery(id+"F0.wireOp",EDGE,"E0.sketch_text.stroke-5"),sQuery(id+"F0.wireOp",EDGE,"E0.sketch_text.stroke-6"),sQuery(id+"F0.wireOp",EDGE,"E0.sketch_text.stroke-7"),sQuery(id+"F0.wireOp",EDGE,"E0.sketch_text.stroke-8")])],"isStart":true});
            var Q136;
            Q136=makeQuery(id+"F1.opExtrude","CAP_FACE",FACE,{"disambiguationData":[OSD([sQuery(id+"F0.wireOp",EDGE,"E0.sketch_text.stroke-0"),sQuery(id+"F0.wireOp",EDGE,"E0.sketch_text.stroke-1"),sQuery(id+"F0.wireOp",EDGE,"E0.sketch_text.stroke-2"),sQuery(id+"F0.wireOp",EDGE,"E0.sketch_text.stroke-3"),sQuery(id+"F0.wireOp",EDGE,"E0.sketch_text.stroke-4"),sQuery(id+"F0.wireOp",EDGE,"E0.sketch_text.stroke-5"),sQuery(id+"F0.wireOp",EDGE,"E0.sketch_text.stroke-6"),sQuery(id+"F0.wireOp",EDGE,"E0.sketch_text.stroke-7"),sQuery(id+"F0.wireOp",EDGE,"E0.sketch_text.stroke-8")])],"isStart":false});
            var Q137;
            Q137=makeQuery(id+"F1.opExtrude","SWEPT_FACE",FACE,{"disambiguationData":[OSD([sQuery(id+"F0.wireOp",EDGE,"E0.sketch_text.stroke-1")])]});
            var Q138;
            Q138=makeQuery(id+"F1.opExtrude","SWEPT_FACE",FACE,{"disambiguationData":[OSD([sQuery(id+"F0.wireOp",EDGE,"E0.sketch_text.stroke-3")])]});
            var Q139;
            Q139=makeQuery(id+"F1.opExtrude","SWEPT_FACE",FACE,{"disambiguationData":[OSD([sQuery(id+"F0.wireOp",EDGE,"E0.sketch_text.stroke-15")])]});
            var Q140;
            Q140=makeQuery(id+"F1.opExtrude","SWEPT_FACE",FACE,{"disambiguationData":[OSD([sQuery(id+"F0.wireOp",EDGE,"E0.sketch_text.stroke-4")])]});
            var Q141;
            Q141=makeQuery(id+"F1.opExtrude","SWEPT_FACE",FACE,{"disambiguationData":[OSD([sQuery(id+"F0.wireOp",EDGE,"E0.sketch_text.stroke-5")])]});
            var Q142;
            Q142=makeQuery(id+"F1.opExtrude","SWEPT_FACE",FACE,{"disambiguationData":[OSD([sQuery(id+"F0.wireOp",EDGE,"E0.sketch_text.stroke-6")])]});
            var Q143;
            Q143=makeQuery(id+"F1.opExtrude","SWEPT_FACE",FACE,{"disambiguationData":[OSD([sQuery(id+"F0.wireOp",EDGE,"E0.sketch_text.stroke-8")])]});
            var Q144;
            Q144=makeQuery(id+"F1.opExtrude","SWEPT_FACE",FACE,{"disambiguationData":[OSD([sQuery(id+"F0.wireOp",EDGE,"E0.sketch_text.stroke-9")])]});
            var Q145;
            Q145=makeQuery(id+"F1.opExtrude","SWEPT_FACE",FACE,{"disambiguationData":[OSD([sQuery(id+"F0.wireOp",EDGE,"E0.sketch_text.stroke-10")])]});
            var Q146;
            Q146=makeQuery(id+"F1.opExtrude","SWEPT_FACE",FACE,{"disambiguationData":[OSD([sQuery(id+"F0.wireOp",EDGE,"E0.sketch_text.stroke-16")])]});
            var Q147;
            Q147=makeQuery(id+"F1.opExtrude","SWEPT_FACE",FACE,{"disambiguationData":[OSD([sQuery(id+"F0.wireOp",EDGE,"E0.sketch_text.stroke-32")])]});
            var Q148;
            Q148=makeQuery(id+"F1.opExtrude","SWEPT_FACE",FACE,{"disambiguationData":[OSD([sQuery(id+"F0.wireOp",EDGE,"E0.sketch_text.stroke-33")])]});
            var Q149;
            Q149=makeQuery(id+"F1.opExtrude","SWEPT_FACE",FACE,{"disambiguationData":[OSD([sQuery(id+"F0.wireOp",EDGE,"E0.sketch_text.stroke-34")])]});
            var Q150;
            Q150=makeQuery(id+"F1.opExtrude","SWEPT_FACE",FACE,{"disambiguationData":[OSD([sQuery(id+"F0.wireOp",EDGE,"E0.sketch_text.stroke-37")])]});
            var Q151;
            Q151=makeQuery(id+"F1.opExtrude","SWEPT_FACE",FACE,{"disambiguationData":[OSD([sQuery(id+"F0.wireOp",EDGE,"E0.sketch_text.stroke-27")])]});
            var Q152;
            Q152=makeQuery(id+"F1.opExtrude","SWEPT_FACE",FACE,{"disambiguationData":[OSD([sQuery(id+"F0.wireOp",EDGE,"E0.sketch_text.stroke-41")])]});
            var Q153;
            Q153=makeQuery(id+"F1.opExtrude","SWEPT_FACE",FACE,{"disambiguationData":[OSD([sQuery(id+"F0.wireOp",EDGE,"E0.sketch_text.stroke-25")])]});
            var Q154;
            Q154=makeQuery(id+"F1.opExtrude","SWEPT_FACE",FACE,{"disambiguationData":[OSD([sQuery(id+"F0.wireOp",EDGE,"E0.sketch_text.stroke-26")])]});
            var Q155;
            Q155=makeQuery(id+"F1.opExtrude","SWEPT_FACE",FACE,{"disambiguationData":[OSD([sQuery(id+"F0.wireOp",EDGE,"E0.sketch_text.stroke-40")])]});
            var Q156;
            Q156=makeQuery(id+"F1.opExtrude","CAP_FACE",FACE,{"disambiguationData":[OSD([sQuery(id+"F0.wireOp",EDGE,"E0.sketch_text.stroke-21"),sQuery(id+"F0.wireOp",EDGE,"E0.sketch_text.stroke-22"),sQuery(id+"F0.wireOp",EDGE,"E0.sketch_text.stroke-23"),sQuery(id+"F0.wireOp",EDGE,"E0.sketch_text.stroke-24"),sQuery(id+"F0.wireOp",EDGE,"E0.sketch_text.stroke-25"),sQuery(id+"F0.wireOp",EDGE,"E0.sketch_text.stroke-26"),sQuery(id+"F0.wireOp",EDGE,"E0.sketch_text.stroke-27"),sQuery(id+"F0.wireOp",EDGE,"E0.sketch_text.stroke-28"),sQuery(id+"F0.wireOp",EDGE,"E0.sketch_text.stroke-29"),sQuery(id+"F0.wireOp",EDGE,"E0.sketch_text.stroke-30"),sQuery(id+"F0.wireOp",EDGE,"E0.sketch_text.stroke-31"),sQuery(id+"F0.wireOp",EDGE,"E0.sketch_text.stroke-32"),sQuery(id+"F0.wireOp",EDGE,"E0.sketch_text.stroke-33")])],"isStart":false});
            var Q157;
            Q157=makeQuery(id+"F1.opExtrude","SWEPT_FACE",FACE,{"disambiguationData":[OSD([sQuery(id+"F0.wireOp",EDGE,"E0.sketch_text.stroke-28")])]});
            var Q158;
            Q158=makeQuery(id+"F1.opExtrude","SWEPT_FACE",FACE,{"disambiguationData":[OSD([sQuery(id+"F0.wireOp",EDGE,"E0.sketch_text.stroke-29")])]});
            var Q159;
            Q159=makeQuery(id+"F1.opExtrude","SWEPT_FACE",FACE,{"disambiguationData":[OSD([sQuery(id+"F0.wireOp",EDGE,"E0.sketch_text.stroke-190")])]});
            var Q160;
            Q160=makeQuery(id+"F1.opExtrude","SWEPT_FACE",FACE,{"disambiguationData":[OSD([sQuery(id+"F0.wireOp",EDGE,"E0.sketch_text.stroke-191")])]});
            var Q161;
            Q161=makeQuery(id+"F1.opExtrude","SWEPT_FACE",FACE,{"disambiguationData":[OSD([sQuery(id+"F0.wireOp",EDGE,"E0.sketch_text.stroke-186")])]});
            var Q162;
            Q162=makeQuery(id+"F1.opExtrude","SWEPT_FACE",FACE,{"disambiguationData":[OSD([sQuery(id+"F0.wireOp",EDGE,"E0.sketch_text.stroke-187")])]});
            var Q163;
            Q163=makeQuery(id+"F1.opExtrude","SWEPT_FACE",FACE,{"disambiguationData":[OSD([sQuery(id+"F0.wireOp",EDGE,"E0.sketch_text.stroke-188")])]});
            var Q164;
            Q164=makeQuery(id+"F1.opExtrude","SWEPT_FACE",FACE,{"disambiguationData":[OSD([sQuery(id+"F0.wireOp",EDGE,"E0.sketch_text.stroke-189")])]});
            var Q165;
            Q165=makeQuery(id+"F1.opExtrude","SWEPT_FACE",FACE,{"disambiguationData":[OSD([sQuery(id+"F0.wireOp",EDGE,"E0.sketch_text.stroke-61")])]});
            var Q166;
            Q166=makeQuery(id+"F1.opExtrude","SWEPT_FACE",FACE,{"disambiguationData":[OSD([sQuery(id+"F0.wireOp",EDGE,"E0.sketch_text.stroke-77")])]});
            var Q167;
            Q167=makeQuery(id+"F1.opExtrude","SWEPT_FACE",FACE,{"disambiguationData":[OSD([sQuery(id+"F0.wireOp",EDGE,"E0.sketch_text.stroke-79")])]});
            var Q168;
            Q168=makeQuery(id+"F1.opExtrude","SWEPT_FACE",FACE,{"disambiguationData":[OSD([sQuery(id+"F0.wireOp",EDGE,"E0.sketch_text.stroke-71")])]});
            var Q169;
            Q169=makeQuery(id+"F1.opExtrude","SWEPT_FACE",FACE,{"disambiguationData":[OSD([sQuery(id+"F0.wireOp",EDGE,"E0.sketch_text.stroke-82")])]});
            var Q170;
            Q170=makeQuery(id+"F1.opExtrude","SWEPT_FACE",FACE,{"disambiguationData":[OSD([sQuery(id+"F0.wireOp",EDGE,"E0.sketch_text.stroke-85")])]});
            var Q171;
            Q171=makeQuery(id+"F1.opExtrude","SWEPT_FACE",FACE,{"disambiguationData":[OSD([sQuery(id+"F0.wireOp",EDGE,"E0.sketch_text.stroke-67")])]});
            var Q172;
            Q172=makeQuery(id+"F1.opExtrude","SWEPT_FACE",FACE,{"disambiguationData":[OSD([sQuery(id+"F0.wireOp",EDGE,"E0.sketch_text.stroke-84")])]});
            var Q173;
            Q173=makeQuery(id+"F1.opExtrude","SWEPT_FACE",FACE,{"disambiguationData":[OSD([sQuery(id+"F0.wireOp",EDGE,"E0.sketch_text.stroke-72")])]});
            var Q174;
            Q174=makeQuery(id+"F1.opExtrude","SWEPT_FACE",FACE,{"disambiguationData":[OSD([sQuery(id+"F0.wireOp",EDGE,"E0.sketch_text.stroke-73")])]});
            var Q175;
            Q175=makeQuery(id+"F1.opExtrude","SWEPT_FACE",FACE,{"disambiguationData":[OSD([sQuery(id+"F0.wireOp",EDGE,"E0.sketch_text.stroke-60")])]});
            var Q176;
            Q176=makeQuery(id+"F1.opExtrude","SWEPT_FACE",FACE,{"disambiguationData":[OSD([sQuery(id+"F0.wireOp",EDGE,"E0.sketch_text.stroke-47")])]});
            var Q177;
            Q177=makeQuery(id+"F1.opExtrude","SWEPT_FACE",FACE,{"disambiguationData":[OSD([sQuery(id+"F0.wireOp",EDGE,"E0.sketch_text.stroke-57")])]});
            var Q178;
            Q178=makeQuery(id+"F1.opExtrude","SWEPT_FACE",FACE,{"disambiguationData":[OSD([sQuery(id+"F0.wireOp",EDGE,"E0.sketch_text.stroke-43")])]});
            var Q179;
            Q179=makeQuery(id+"F1.opExtrude","SWEPT_FACE",FACE,{"disambiguationData":[OSD([sQuery(id+"F0.wireOp",EDGE,"E0.sketch_text.stroke-58")])]});
            var Q180;
            Q180=makeQuery(id+"F1.opExtrude","SWEPT_FACE",FACE,{"disambiguationData":[OSD([sQuery(id+"F0.wireOp",EDGE,"E0.sketch_text.stroke-59")])]});
            var Q181;
            Q181=makeQuery(id+"F1.opExtrude","SWEPT_FACE",FACE,{"disambiguationData":[OSD([sQuery(id+"F0.wireOp",EDGE,"E0.sketch_text.stroke-45")])]});
            var Q182;
            Q182=makeQuery(id+"F1.opExtrude","SWEPT_FACE",FACE,{"disambiguationData":[OSD([sQuery(id+"F0.wireOp",EDGE,"E0.sketch_text.stroke-24")])]});
            var Q183;
            Q183=makeQuery(id+"F1.opExtrude","SWEPT_FACE",FACE,{"disambiguationData":[OSD([sQuery(id+"F0.wireOp",EDGE,"E0.sketch_text.stroke-17")])]});
            var Q184;
            Q184=makeQuery(id+"F1.opExtrude","SWEPT_FACE",FACE,{"disambiguationData":[OSD([sQuery(id+"F0.wireOp",EDGE,"E0.sketch_text.stroke-36")])]});
            var Q185;
            Q185=makeQuery(id+"F1.opExtrude","SWEPT_FACE",FACE,{"disambiguationData":[OSD([sQuery(id+"F0.wireOp",EDGE,"E0.sketch_text.stroke-38")])]});
            var Q186;
            Q186=makeQuery(id+"F1.opExtrude","SWEPT_FACE",FACE,{"disambiguationData":[OSD([sQuery(id+"F0.wireOp",EDGE,"E0.sketch_text.stroke-74")])]});
            var Q187;
            Q187=makeQuery(id+"F1.opExtrude","SWEPT_FACE",FACE,{"disambiguationData":[OSD([sQuery(id+"F0.wireOp",EDGE,"E0.sketch_text.stroke-75")])]});
            var Q188;
            Q188=makeQuery(id+"F1.opExtrude","SWEPT_FACE",FACE,{"disambiguationData":[OSD([sQuery(id+"F0.wireOp",EDGE,"E0.sketch_text.stroke-95")])]});
            var Q189;
            Q189=makeQuery(id+"F1.opExtrude","SWEPT_FACE",FACE,{"disambiguationData":[OSD([sQuery(id+"F0.wireOp",EDGE,"E0.sketch_text.stroke-2")])]});
            var Q190;
            Q190=makeQuery(id+"F1.opExtrude","SWEPT_FACE",FACE,{"disambiguationData":[OSD([sQuery(id+"F0.wireOp",EDGE,"E0.sketch_text.stroke-12")])]});
            var Q191;
            Q191=makeQuery(id+"F1.opExtrude","CAP_FACE",FACE,{"disambiguationData":[OSD([sQuery(id+"F0.wireOp",EDGE,"E0.sketch_text.stroke-9"),sQuery(id+"F0.wireOp",EDGE,"E0.sketch_text.stroke-10"),sQuery(id+"F0.wireOp",EDGE,"E0.sketch_text.stroke-11"),sQuery(id+"F0.wireOp",EDGE,"E0.sketch_text.stroke-12")])],"isStart":false});
            var Q192;
            Q192=makeQuery(id+"F1.opExtrude","SWEPT_FACE",FACE,{"disambiguationData":[OSD([sQuery(id+"F0.wireOp",EDGE,"E0.sketch_text.stroke-197")])]});
            var Q193;
            Q193=makeQuery(id+"F1.opExtrude","SWEPT_FACE",FACE,{"disambiguationData":[OSD([sQuery(id+"F0.wireOp",EDGE,"E0.sketch_text.stroke-199")])]});
            var Q194;
            Q194=makeQuery(id+"F1.opExtrude","CAP_FACE",FACE,{"disambiguationData":[OSD([sQuery(id+"F0.wireOp",EDGE,"E0.sketch_text.stroke-190"),sQuery(id+"F0.wireOp",EDGE,"E0.sketch_text.stroke-191"),sQuery(id+"F0.wireOp",EDGE,"E0.sketch_text.stroke-192"),sQuery(id+"F0.wireOp",EDGE,"E0.sketch_text.stroke-193"),sQuery(id+"F0.wireOp",EDGE,"E0.sketch_text.stroke-194"),sQuery(id+"F0.wireOp",EDGE,"E0.sketch_text.stroke-195"),sQuery(id+"F0.wireOp",EDGE,"E0.sketch_text.stroke-196"),sQuery(id+"F0.wireOp",EDGE,"E0.sketch_text.stroke-197"),sQuery(id+"F0.wireOp",EDGE,"E0.sketch_text.stroke-198"),sQuery(id+"F0.wireOp",EDGE,"E0.sketch_text.stroke-199"),sQuery(id+"F0.wireOp",EDGE,"E0.sketch_text.stroke-200"),sQuery(id+"F0.wireOp",EDGE,"E0.sketch_text.stroke-201"),sQuery(id+"F0.wireOp",EDGE,"E0.sketch_text.stroke-202"),sQuery(id+"F0.wireOp",EDGE,"E0.sketch_text.stroke-203"),sQuery(id+"F0.wireOp",EDGE,"E0.sketch_text.stroke-204"),sQuery(id+"F0.wireOp",EDGE,"E0.sketch_text.stroke-205")])],"isStart":false});
            var Q195;
            Q195=makeQuery(id+"F1.opExtrude","SWEPT_FACE",FACE,{"disambiguationData":[OSD([sQuery(id+"F0.wireOp",EDGE,"E0.sketch_text.stroke-192")])]});
            var Q196;
            Q196=makeQuery(id+"F1.opExtrude","SWEPT_FACE",FACE,{"disambiguationData":[OSD([sQuery(id+"F0.wireOp",EDGE,"E0.sketch_text.stroke-203")])]});
            var Q197;
            Q197=makeQuery(id+"F1.opExtrude","SWEPT_FACE",FACE,{"disambiguationData":[OSD([sQuery(id+"F0.wireOp",EDGE,"E0.sketch_text.stroke-205")])]});
            var Q198;
            Q198=makeQuery(id+"F1.opExtrude","CAP_FACE",FACE,{"disambiguationData":[OSD([sQuery(id+"F0.wireOp",EDGE,"E0.sketch_text.stroke-13"),sQuery(id+"F0.wireOp",EDGE,"E0.sketch_text.stroke-14"),sQuery(id+"F0.wireOp",EDGE,"E0.sketch_text.stroke-15"),sQuery(id+"F0.wireOp",EDGE,"E0.sketch_text.stroke-16"),sQuery(id+"F0.wireOp",EDGE,"E0.sketch_text.stroke-17"),sQuery(id+"F0.wireOp",EDGE,"E0.sketch_text.stroke-18"),sQuery(id+"F0.wireOp",EDGE,"E0.sketch_text.stroke-19"),sQuery(id+"F0.wireOp",EDGE,"E0.sketch_text.stroke-20")])],"isStart":false});
            var Q199;
            Q199=makeQuery(id+"F1.opExtrude","SWEPT_FACE",FACE,{"disambiguationData":[OSD([sQuery(id+"F0.wireOp",EDGE,"E0.sketch_text.stroke-97")])]});
            var Q200;
            Q200=makeQuery(id+"F1.opExtrude","SWEPT_FACE",FACE,{"disambiguationData":[OSD([sQuery(id+"F0.wireOp",EDGE,"E0.sketch_text.stroke-96")])]});
            var Q201;
            Q201=makeQuery(id+"F1.opExtrude","SWEPT_FACE",FACE,{"disambiguationData":[OSD([sQuery(id+"F0.wireOp",EDGE,"E0.sketch_text.stroke-86")])]});
            var Q202;
            Q202=makeQuery(id+"F1.opExtrude","SWEPT_FACE",FACE,{"disambiguationData":[OSD([sQuery(id+"F0.wireOp",EDGE,"E0.sketch_text.stroke-0")])]});
            var Q203;
            Q203=makeQuery(id+"F1.opExtrude","SWEPT_FACE",FACE,{"disambiguationData":[OSD([sQuery(id+"F0.wireOp",EDGE,"E0.sketch_text.stroke-204")])]});
            var Q204;
            Q204=makeQuery(id+"F1.opExtrude","SWEPT_FACE",FACE,{"disambiguationData":[OSD([sQuery(id+"F0.wireOp",EDGE,"E0.sketch_text.stroke-30")])]});
            var Q205;
            Q205=makeQuery(id+"F1.opExtrude","SWEPT_FACE",FACE,{"disambiguationData":[OSD([sQuery(id+"F0.wireOp",EDGE,"E0.sketch_text.stroke-7")])]});
            var Q206;
            Q206=makeQuery(id+"F1.opExtrude","CAP_FACE",FACE,{"disambiguationData":[OSD([sQuery(id+"F0.wireOp",EDGE,"E0.sketch_text.stroke-9"),sQuery(id+"F0.wireOp",EDGE,"E0.sketch_text.stroke-10"),sQuery(id+"F0.wireOp",EDGE,"E0.sketch_text.stroke-11"),sQuery(id+"F0.wireOp",EDGE,"E0.sketch_text.stroke-12")])],"isStart":true});
            var Q207;
            Q207=makeQuery(id+"F1.opExtrude","CAP_FACE",FACE,{"disambiguationData":[OSD([sQuery(id+"F0.wireOp",EDGE,"E0.sketch_text.stroke-166"),sQuery(id+"F0.wireOp",EDGE,"E0.sketch_text.stroke-167"),sQuery(id+"F0.wireOp",EDGE,"E0.sketch_text.stroke-168"),sQuery(id+"F0.wireOp",EDGE,"E0.sketch_text.stroke-169"),sQuery(id+"F0.wireOp",EDGE,"E0.sketch_text.stroke-170"),sQuery(id+"F0.wireOp",EDGE,"E0.sketch_text.stroke-171"),sQuery(id+"F0.wireOp",EDGE,"E0.sketch_text.stroke-172"),sQuery(id+"F0.wireOp",EDGE,"E0.sketch_text.stroke-173"),sQuery(id+"F0.wireOp",EDGE,"E0.sketch_text.stroke-174"),sQuery(id+"F0.wireOp",EDGE,"E0.sketch_text.stroke-175"),sQuery(id+"F0.wireOp",EDGE,"E0.sketch_text.stroke-176"),sQuery(id+"F0.wireOp",EDGE,"E0.sketch_text.stroke-177"),sQuery(id+"F0.wireOp",EDGE,"E0.sketch_text.stroke-178"),sQuery(id+"F0.wireOp",EDGE,"E0.sketch_text.stroke-179"),sQuery(id+"F0.wireOp",EDGE,"E0.sketch_text.stroke-180"),sQuery(id+"F0.wireOp",EDGE,"E0.sketch_text.stroke-181"),sQuery(id+"F0.wireOp",EDGE,"E0.sketch_text.stroke-182"),sQuery(id+"F0.wireOp",EDGE,"E0.sketch_text.stroke-183"),sQuery(id+"F0.wireOp",EDGE,"E0.sketch_text.stroke-184"),sQuery(id+"F0.wireOp",EDGE,"E0.sketch_text.stroke-185"),sQuery(id+"F0.wireOp",EDGE,"E0.sketch_text.stroke-186"),sQuery(id+"F0.wireOp",EDGE,"E0.sketch_text.stroke-187"),sQuery(id+"F0.wireOp",EDGE,"E0.sketch_text.stroke-188"),sQuery(id+"F0.wireOp",EDGE,"E0.sketch_text.stroke-189")])],"isStart":true});
            var Q208;
            Q208=makeQuery(id+"F1.opExtrude","SWEPT_FACE",FACE,{"disambiguationData":[OSD([sQuery(id+"F0.wireOp",EDGE,"E0.sketch_text.stroke-39")])]});
            var Q209;
            Q209=makeQuery(id+"F1.opExtrude","CAP_FACE",FACE,{"disambiguationData":[OSD([sQuery(id+"F0.wireOp",EDGE,"E0.sketch_text.stroke-190"),sQuery(id+"F0.wireOp",EDGE,"E0.sketch_text.stroke-191"),sQuery(id+"F0.wireOp",EDGE,"E0.sketch_text.stroke-192"),sQuery(id+"F0.wireOp",EDGE,"E0.sketch_text.stroke-193"),sQuery(id+"F0.wireOp",EDGE,"E0.sketch_text.stroke-194"),sQuery(id+"F0.wireOp",EDGE,"E0.sketch_text.stroke-195"),sQuery(id+"F0.wireOp",EDGE,"E0.sketch_text.stroke-196"),sQuery(id+"F0.wireOp",EDGE,"E0.sketch_text.stroke-197"),sQuery(id+"F0.wireOp",EDGE,"E0.sketch_text.stroke-198"),sQuery(id+"F0.wireOp",EDGE,"E0.sketch_text.stroke-199"),sQuery(id+"F0.wireOp",EDGE,"E0.sketch_text.stroke-200"),sQuery(id+"F0.wireOp",EDGE,"E0.sketch_text.stroke-201"),sQuery(id+"F0.wireOp",EDGE,"E0.sketch_text.stroke-202"),sQuery(id+"F0.wireOp",EDGE,"E0.sketch_text.stroke-203"),sQuery(id+"F0.wireOp",EDGE,"E0.sketch_text.stroke-204"),sQuery(id+"F0.wireOp",EDGE,"E0.sketch_text.stroke-205")])],"isStart":true});
            var Q210;
            Q210=makeQuery(id+"F1.opExtrude","SWEPT_FACE",FACE,{"disambiguationData":[OSD([sQuery(id+"F0.wireOp",EDGE,"E0.sketch_text.stroke-196")])]});
            var Q211;
            Q211=makeQuery(id+"F1.opExtrude","CAP_FACE",FACE,{"disambiguationData":[OSD([sQuery(id+"F0.wireOp",EDGE,"E0.sketch_text.stroke-21"),sQuery(id+"F0.wireOp",EDGE,"E0.sketch_text.stroke-22"),sQuery(id+"F0.wireOp",EDGE,"E0.sketch_text.stroke-23"),sQuery(id+"F0.wireOp",EDGE,"E0.sketch_text.stroke-24"),sQuery(id+"F0.wireOp",EDGE,"E0.sketch_text.stroke-25"),sQuery(id+"F0.wireOp",EDGE,"E0.sketch_text.stroke-26"),sQuery(id+"F0.wireOp",EDGE,"E0.sketch_text.stroke-27"),sQuery(id+"F0.wireOp",EDGE,"E0.sketch_text.stroke-28"),sQuery(id+"F0.wireOp",EDGE,"E0.sketch_text.stroke-29"),sQuery(id+"F0.wireOp",EDGE,"E0.sketch_text.stroke-30"),sQuery(id+"F0.wireOp",EDGE,"E0.sketch_text.stroke-31"),sQuery(id+"F0.wireOp",EDGE,"E0.sketch_text.stroke-32"),sQuery(id+"F0.wireOp",EDGE,"E0.sketch_text.stroke-33")])],"isStart":true});
            var Q212;
            Q212=makeQuery(id+"F1.opExtrude","SWEPT_FACE",FACE,{"disambiguationData":[OSD([sQuery(id+"F0.wireOp",EDGE,"E0.sketch_text.stroke-198")])]});
            var Q213;
            Q213=makeQuery(id+"F1.opExtrude","SWEPT_FACE",FACE,{"disambiguationData":[OSD([sQuery(id+"F0.wireOp",EDGE,"E0.sketch_text.stroke-201")])]});
            var Q214;
            Q214=makeQuery(id+"F1.opExtrude","SWEPT_FACE",FACE,{"disambiguationData":[OSD([sQuery(id+"F0.wireOp",EDGE,"E0.sketch_text.stroke-200")])]});
            var Q215;
            Q215=makeQuery(id+"F1.opExtrude","SWEPT_FACE",FACE,{"disambiguationData":[OSD([sQuery(id+"F0.wireOp",EDGE,"E0.sketch_text.stroke-202")])]});
            var Q216;
            Q216=makeQuery(id+"F1.opExtrude","SWEPT_FACE",FACE,{"disambiguationData":[OSD([sQuery(id+"F0.wireOp",EDGE,"E0.sketch_text.stroke-21")])]});
            var Q217;
            Q217=makeQuery(id+"F1.opExtrude","SWEPT_FACE",FACE,{"disambiguationData":[OSD([sQuery(id+"F0.wireOp",EDGE,"E0.sketch_text.stroke-78")])]});
            var Q218;
            Q218=makeQuery(id+"F1.opExtrude","SWEPT_FACE",FACE,{"disambiguationData":[OSD([sQuery(id+"F0.wireOp",EDGE,"E0.sketch_text.stroke-22")])]});
            var Q219;
            Q219=makeQuery(id+"F1.opExtrude","SWEPT_FACE",FACE,{"disambiguationData":[OSD([sQuery(id+"F0.wireOp",EDGE,"E0.sketch_text.stroke-70")])]});
            var Q220;
            Q220=makeQuery(id+"F1.opExtrude","SWEPT_FACE",FACE,{"disambiguationData":[OSD([sQuery(id+"F0.wireOp",EDGE,"E0.sketch_text.stroke-14")])]});
            var Q221;
            Q221=makeQuery(id+"F1.opExtrude","SWEPT_FACE",FACE,{"disambiguationData":[OSD([sQuery(id+"F0.wireOp",EDGE,"E0.sketch_text.stroke-19")])]});
            var Q222;
            Q222=makeQuery(id+"F1.opExtrude","CAP_FACE",FACE,{"disambiguationData":[OSD([sQuery(id+"F0.wireOp",EDGE,"E0.sketch_text.stroke-13"),sQuery(id+"F0.wireOp",EDGE,"E0.sketch_text.stroke-14"),sQuery(id+"F0.wireOp",EDGE,"E0.sketch_text.stroke-15"),sQuery(id+"F0.wireOp",EDGE,"E0.sketch_text.stroke-16"),sQuery(id+"F0.wireOp",EDGE,"E0.sketch_text.stroke-17"),sQuery(id+"F0.wireOp",EDGE,"E0.sketch_text.stroke-18"),sQuery(id+"F0.wireOp",EDGE,"E0.sketch_text.stroke-19"),sQuery(id+"F0.wireOp",EDGE,"E0.sketch_text.stroke-20")])],"isStart":true});
            var Q223;
            Q223=makeQuery(id+"F1.opExtrude","SWEPT_FACE",FACE,{"disambiguationData":[OSD([sQuery(id+"F0.wireOp",EDGE,"E0.sketch_text.stroke-42")])]});
            var Q224;
            Q224=makeQuery(id+"F1.opExtrude","SWEPT_FACE",FACE,{"disambiguationData":[OSD([sQuery(id+"F0.wireOp",EDGE,"E0.sketch_text.stroke-20")])]});
            var Q225;
            Q225=makeQuery(id+"F1.opExtrude","SWEPT_FACE",FACE,{"disambiguationData":[OSD([sQuery(id+"F0.wireOp",EDGE,"E0.sketch_text.stroke-31")])]});
            var Q226;
            Q226=makeQuery(id+"F1.opExtrude","SWEPT_FACE",FACE,{"disambiguationData":[OSD([sQuery(id+"F0.wireOp",EDGE,"E0.sketch_text.stroke-81")])]});
            var Q227;
            Q227=makeQuery(id+"F1.opExtrude","SWEPT_FACE",FACE,{"disambiguationData":[OSD([sQuery(id+"F0.wireOp",EDGE,"E0.sketch_text.stroke-35")])]});
            var Q228;
            Q228=makeQuery(id+"F1.opExtrude","SWEPT_FACE",FACE,{"disambiguationData":[OSD([sQuery(id+"F0.wireOp",EDGE,"E0.sketch_text.stroke-52")])]});
            var Q229;
            Q229=qCreatedBy(makeId("Right.planeOp"),FACE);
            mirror(context, id + "F2", {"entities" : qUnion([Q0]), "faces" : qUnion([Q1, Q2, Q3, Q4, Q5, Q6, Q7, Q8, Q9, Q10, Q11, Q12, Q13, Q14, Q15, Q16, Q17, Q18, Q19, Q20, Q21, Q22, Q23, Q24, Q25, Q26, Q27, Q28, Q29, Q30, Q31, Q32, Q33, Q34, Q35, Q36, Q37, Q38, Q39, Q40, Q41, Q42, Q43, Q44, Q45, Q46, Q47, Q48, Q49, Q50, Q51, Q52, Q53, Q54, Q55, Q56, Q57, Q58, Q59, Q60, Q61, Q62, Q63, Q64, Q65, Q66, Q67, Q68, Q69, Q70, Q71, Q72, Q73, Q74, Q75, Q76, Q77, Q78, Q79, Q80, Q81, Q82, Q83, Q84, Q85, Q86, Q87, Q88, Q89, Q90, Q91, Q92, Q93, Q94, Q95, Q96, Q97, Q98, Q99, Q100, Q101, Q102, Q103, Q104, Q105, Q106, Q107, Q108, Q109, Q110, Q111, Q112, Q113, Q114, Q115, Q116, Q117, Q118, Q119, Q120, Q121, Q122, Q123, Q124, Q125, Q126, Q127, Q128, Q129, Q130, Q131, Q132, Q133, Q134, Q135, Q136, Q137, Q138, Q139, Q140, Q141, Q142, Q143, Q144, Q145, Q146, Q147, Q148, Q149, Q150, Q151, Q152, Q153, Q154, Q155, Q156, Q157, Q158, Q159, Q160, Q161, Q162, Q163, Q164, Q165, Q166, Q167, Q168, Q169, Q170, Q171, Q172, Q173, Q174, Q175, Q176, Q177, Q178, Q179, Q180, Q181, Q182, Q183, Q184, Q185, Q186, Q187, Q188, Q189, Q190, Q191, Q192, Q193, Q194, Q195, Q196, Q197, Q198, Q199, Q200, Q201, Q202, Q203, Q204, Q205, Q206, Q207, Q208, Q209, Q210, Q211, Q212, Q213, Q214, Q215, Q216, Q217, Q218, Q219, Q220, Q221, Q222, Q223, Q224, Q225, Q226, Q227, Q228]), "mirrorPlane" : qUnion([Q229]), "patternType" : MirrorType.FACE});
        }
    });
